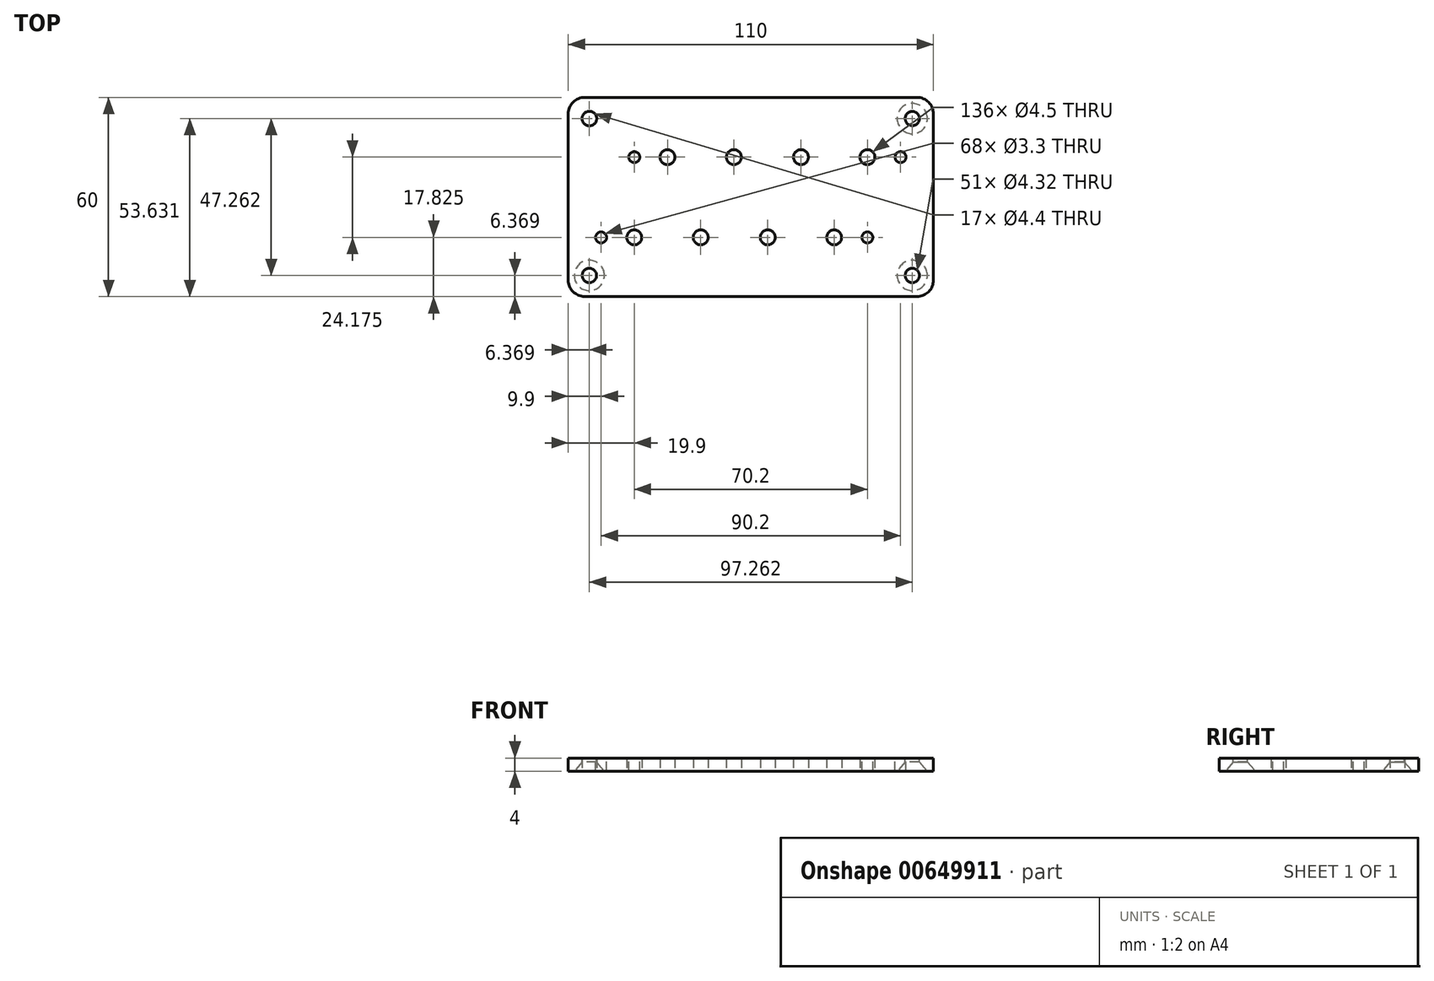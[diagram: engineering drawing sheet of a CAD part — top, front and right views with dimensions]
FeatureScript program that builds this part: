
annotation { "Feature Type Name" : "Feature", "Feature Type Description" : "" }
export const myFeature = defineFeature(function(context is Context, id is Id, definition is map)
    precondition{}
    {
        {
            var Q0;
            Q0=qCreatedBy(makeId("Top.planeOp"),FACE);
            var sketch = newSketch(context, id + "F0", { "sketchPlane" : qUnion([Q0])});
            skPoint(sketch, "E0.middle", {"position": v(5, 12) * mm});
            skCircle(sketch, "E1.MirrorC", {"center": v(-35.1, 12) * mm, "radius": 1.75 * mm});
            skLineSegment(sketch, "E2.bottom", {"start": v(40.1, 22) * mm, "end": v(-30.1, 22) * mm});
            skLineSegment(sketch, "E2.top", {"start": v(40.1, 2) * mm, "end": v(-30.1, 2) * mm});
            skLineSegment(sketch, "E2.left", {"start": v(46.36, 18.13) * mm, "end": v(46.36, 18.13) * mm});
            skLineSegment(sketch, "E2.right", {"start": v(-43.84, 18.13) * mm, "end": v(-43.84, 18.13) * mm});
            skPoint(sketch, "E3.visualSharp", {"position": v(50.1, 22) * mm});
            skArc(sketch, "E3.filletArc", {"start": v(50.1, 12) * mm, "mid": v(47.17, 19.07) * mm, "end": v(40.1, 22) * mm});
            skPoint(sketch, "E4.visualSharp", {"position": v(50.1, 2) * mm});
            skArc(sketch, "E4.filletArc", {"start": v(40.1, 2) * mm, "mid": v(47.17, 4.93) * mm, "end": v(50.1, 12) * mm});
            skPoint(sketch, "E5.visualSharp", {"position": v(-40.1, 2) * mm});
            skArc(sketch, "E5.filletArc", {"start": v(-40.1, 12) * mm, "mid": v(-37.17, 4.93) * mm, "end": v(-30.1, 2) * mm});
            skPoint(sketch, "E6.visualSharp", {"position": v(-40.1, 22) * mm});
            skArc(sketch, "E6.filletArc", {"start": v(-30.1, 22) * mm, "mid": v(-37.17, 19.07) * mm, "end": v(-40.1, 12) * mm});
            skCircle(sketch, "E7", {"center": v(-25.1, 12) * mm, "radius": 2.25 * mm});
            skCircle(sketch, "E8", {"center": v(-5.1, 12) * mm, "radius": 2.25 * mm});
            skCircle(sketch, "E9.MirrorC", {"center": v(35.1, 12) * mm, "radius": 2.25 * mm});
            skCircle(sketch, "E10.MirrorC", {"center": v(45.1, 12) * mm, "radius": 1.75 * mm});
            skCircle(sketch, "E11.MirrorC", {"center": v(15.1, 12) * mm, "radius": 2.25 * mm});
            skPoint(sketch, "E12.middle", {"position": v(-5, -12.18) * mm});
            skCircle(sketch, "E13.MirrorC", {"center": v(-45.1, -12.18) * mm, "radius": 1.75 * mm});
            skLineSegment(sketch, "E14.bottom", {"start": v(30.1, -2.18) * mm, "end": v(-40.1, -2.18) * mm});
            skLineSegment(sketch, "E14.top", {"start": v(30.1, -22.18) * mm, "end": v(-40.1, -22.18) * mm});
            skLineSegment(sketch, "E14.right", {"start": v(14.58, -2.05) * mm, "end": v(14.58, -2.05) * mm});
            skPoint(sketch, "E15.visualSharp", {"position": v(40.1, -2.18) * mm});
            skArc(sketch, "E15.filletArc", {"start": v(40.1, -12.18) * mm, "mid": v(37.17, -5.1) * mm, "end": v(30.1, -2.18) * mm});
            skPoint(sketch, "E16.visualSharp", {"position": v(40.1, -22.18) * mm});
            skArc(sketch, "E16.filletArc", {"start": v(30.1, -22.18) * mm, "mid": v(37.17, -19.25) * mm, "end": v(40.1, -12.18) * mm});
            skPoint(sketch, "E17.visualSharp", {"position": v(-50.1, -22.18) * mm});
            skArc(sketch, "E17.filletArc", {"start": v(-50.1, -12.18) * mm, "mid": v(-47.17, -19.25) * mm, "end": v(-40.1, -22.18) * mm});
            skPoint(sketch, "E18.visualSharp", {"position": v(-50.1, -2.18) * mm});
            skArc(sketch, "E18.filletArc", {"start": v(-40.1, -2.18) * mm, "mid": v(-47.17, -5.1) * mm, "end": v(-50.1, -12.18) * mm});
            skCircle(sketch, "E19", {"center": v(-35.1, -12.18) * mm, "radius": 2.25 * mm});
            skCircle(sketch, "E20", {"center": v(-15.1, -12.18) * mm, "radius": 2.25 * mm});
            skCircle(sketch, "E21.MirrorC", {"center": v(25.1, -12.18) * mm, "radius": 2.25 * mm});
            skCircle(sketch, "E22.MirrorC", {"center": v(35.1, -12.18) * mm, "radius": 1.75 * mm});
            skCircle(sketch, "E23.MirrorC", {"center": v(5.1, -12.18) * mm, "radius": 2.25 * mm});
            skLineSegment(sketch, "E24.bottom", {"start": v(50, 30) * mm, "end": v(-50, 30) * mm});
            skLineSegment(sketch, "E24.top", {"start": v(50, -30) * mm, "end": v(-50, -30) * mm});
            skLineSegment(sketch, "E24.left", {"start": v(55, 25) * mm, "end": v(55, -25) * mm});
            skLineSegment(sketch, "E24.right", {"start": v(-55, 25) * mm, "end": v(-55, -25) * mm});
            skPoint(sketch, "E24.middle", {"position": v(0, 0) * mm});
            skCircle(sketch, "E25", {"center": v(48.63, 23.63) * mm, "radius": 3.97 * mm});
            skCircle(sketch, "E26", {"center": v(48.63, 23.63) * mm, "radius": 2.2 * mm});
            skLineSegment(sketch, "E27", {"start": v(52.6, 23.63) * mm, "end": v(55, 23.63) * mm});
            skLineSegment(sketch, "E28", {"start": v(48.63, 27.6) * mm, "end": v(48.63, 30) * mm});
            skCircle(sketch, "E29.MirrorC", {"center": v(-48.63, 23.63) * mm, "radius": 3.97 * mm});
            skCircle(sketch, "E30.MirrorC", {"center": v(-48.63, 23.63) * mm, "radius": 2.2 * mm});
            skCircle(sketch, "E31.MirrorC", {"center": v(-48.63, -23.63) * mm, "radius": 2.2 * mm});
            skCircle(sketch, "E32.MirrorC", {"center": v(-48.63, -23.63) * mm, "radius": 3.97 * mm});
            skCircle(sketch, "E33.MirrorC", {"center": v(48.63, -23.63) * mm, "radius": 2.2 * mm});
            skCircle(sketch, "E34.MirrorC", {"center": v(48.63, -23.63) * mm, "radius": 3.97 * mm});
            skPoint(sketch, "E35.visualSharp", {"position": v(-55, 30) * mm});
            skArc(sketch, "E35.filletArc", {"start": v(-50, 30) * mm, "mid": v(-53.54, 28.54) * mm, "end": v(-55, 25) * mm});
            skPoint(sketch, "E36.visualSharp", {"position": v(55, 30) * mm});
            skArc(sketch, "E36.filletArc", {"start": v(55, 25) * mm, "mid": v(53.54, 28.54) * mm, "end": v(50, 30) * mm});
            skPoint(sketch, "E37.visualSharp", {"position": v(55, -30) * mm});
            skArc(sketch, "E37.filletArc", {"start": v(50, -30) * mm, "mid": v(53.54, -28.54) * mm, "end": v(55, -25) * mm});
            skPoint(sketch, "E38.visualSharp", {"position": v(-55, -30) * mm});
            skArc(sketch, "E38.filletArc", {"start": v(-55, -25) * mm, "mid": v(-53.54, -28.54) * mm, "end": v(-50, -30) * mm});
            skSolve(sketch);
        }
        {
            var Q0;
            Q0 = qSketchRegion(id + "F0", true);
            var Q1;
            Q1=makeQuery(id+"F0.imprint","IMPRINT",FACE,{"disambiguationData":[TD([[makeQuery(id+"F0.imprint","IMPRINT",EDGE,{"derivedFrom":sQuery(id+"F0.wireOp",EDGE,"E29.MirrorC")}),-1.0]])]});
            var Q2;
            Q2=makeQuery(id+"F0.imprint","IMPRINT",FACE,{"disambiguationData":[TD([[makeQuery(id+"F0.imprint","IMPRINT",EDGE,{"derivedFrom":sQuery(id+"F0.wireOp",EDGE,"E26")}),-1.0]])]});
            var Q3;
            Q3=makeQuery(id+"F0.imprint","IMPRINT",FACE,{"disambiguationData":[TD([[makeQuery(id+"F0.imprint","IMPRINT",EDGE,{"derivedFrom":sQuery(id+"F0.wireOp",EDGE,"E1.MirrorC")}),1.0]])]});
            var Q4;
            Q4=makeQuery(id+"F0.imprint","IMPRINT",FACE,{"disambiguationData":[TD([[makeQuery(id+"F0.imprint","IMPRINT",EDGE,{"derivedFrom":sQuery(id+"F0.wireOp",EDGE,"E13.MirrorC")}),1.0]])]});
            var Q5;
            Q5=makeQuery(id+"F0.imprint","IMPRINT",FACE,{"disambiguationData":[TD([[makeQuery(id+"F0.imprint","IMPRINT",EDGE,{"derivedFrom":sQuery(id+"F0.wireOp",EDGE,"E31.MirrorC")}),-1.0]])]});
            var Q6;
            Q6=makeQuery(id+"F0.imprint","IMPRINT",FACE,{"disambiguationData":[TD([[makeQuery(id+"F0.imprint","IMPRINT",EDGE,{"derivedFrom":sQuery(id+"F0.wireOp",EDGE,"E33.MirrorC")}),1.0]])]});
            var Q7;
            Q7=makeQuery(id+"F0.imprint","IMPRINT",FACE,{"disambiguationData":[TD([[makeQuery(id+"F0.imprint","IMPRINT",EDGE,{"derivedFrom":sQuery(id+"F0.wireOp",EDGE,"E31.MirrorC")}),1.0]])]});
            var Q8;
            Q8=makeQuery(id+"F0.imprint","IMPRINT",FACE,{"disambiguationData":[TD([[makeQuery(id+"F0.imprint","IMPRINT",EDGE,{"derivedFrom":sQuery(id+"F0.wireOp",EDGE,"E33.MirrorC")}),-1.0]])]});
            var Q9;
            Q9=makeQuery(id+"F0.imprint","IMPRINT",FACE,{"disambiguationData":[TD([[makeQuery(id+"F0.imprint","IMPRINT",EDGE,{"derivedFrom":sQuery(id+"F0.wireOp",EDGE,"E30.MirrorC")}),-1.0]])]});
            var Q10;
            Q10=makeQuery(id+"F0.imprint","IMPRINT",FACE,{"disambiguationData":[TD([[makeQuery(id+"F0.imprint","IMPRINT",EDGE,{"derivedFrom":sQuery(id+"F0.wireOp",EDGE,"E26")}),1.0]])]});
            var Q11;
            Q11=makeQuery(id+"F0.imprint","IMPRINT",FACE,{"disambiguationData":[TD([[makeQuery(id+"F0.imprint","IMPRINT",EDGE,{"derivedFrom":sQuery(id+"F0.wireOp",EDGE,"E10.MirrorC")}),1.0]])]});
            var Q12;
            Q12=makeQuery(id+"F0.imprint","IMPRINT",FACE,{"disambiguationData":[TD([[makeQuery(id+"F0.imprint","IMPRINT",EDGE,{"derivedFrom":sQuery(id+"F0.wireOp",EDGE,"E1.MirrorC")}),-1.0]])]});
            var Q13;
            Q13=makeQuery(id+"F0.imprint","IMPRINT",FACE,{"disambiguationData":[TD([[makeQuery(id+"F0.imprint","IMPRINT",EDGE,{"derivedFrom":sQuery(id+"F0.wireOp",EDGE,"E13.MirrorC")}),-1.0]])]});
            var Q14;
            Q14=makeQuery(id+"F0.imprint","IMPRINT",FACE,{"disambiguationData":[TD([[makeQuery(id+"F0.imprint","IMPRINT",EDGE,{"derivedFrom":sQuery(id+"F0.wireOp",EDGE,"E22.MirrorC")}),1.0]])]});
            extrude(context, id + "F1", {"entities" : qUnion([Q0, Q1, Q2, Q3, Q4, Q5, Q6, Q7, Q8, Q9, Q10, Q11, Q12, Q13, Q14]), "depth" : 4 * mm, "offsetDistance" : 25 * mm});
        }
        {
            var Q0;
            Q0=sQuery(id+"F0.wireOp",VERTEX,"E29.MirrorC.center");
            var Q1;
            Q1=sQuery(id+"F0.wireOp",VERTEX,"E31.MirrorC.center");
            var Q2;
            Q2=sQuery(id+"F0.wireOp",VERTEX,"E25.center");
            var Q3;
            Q3=sQuery(id+"F0.wireOp",VERTEX,"E33.MirrorC.center");
            var Q4;
            Q4=makeQuery(id+"F1.opExtrude","SWEPT_BODY",BODY,{"disambiguationData":[OSD([sQuery(id+"F0.wireOp",EDGE,"E1.MirrorC"),sQuery(id+"F0.wireOp",EDGE,"E7"),sQuery(id+"F0.wireOp",EDGE,"E8"),sQuery(id+"F0.wireOp",EDGE,"E9.MirrorC"),sQuery(id+"F0.wireOp",EDGE,"E10.MirrorC"),sQuery(id+"F0.wireOp",EDGE,"E11.MirrorC"),sQuery(id+"F0.wireOp",EDGE,"E13.MirrorC"),sQuery(id+"F0.wireOp",EDGE,"E19"),sQuery(id+"F0.wireOp",EDGE,"E20"),sQuery(id+"F0.wireOp",EDGE,"E21.MirrorC"),sQuery(id+"F0.wireOp",EDGE,"E22.MirrorC"),sQuery(id+"F0.wireOp",EDGE,"E23.MirrorC"),sQuery(id+"F0.wireOp",EDGE,"E24.bottom"),sQuery(id+"F0.wireOp",EDGE,"E24.top"),sQuery(id+"F0.wireOp",EDGE,"E24.left"),sQuery(id+"F0.wireOp",EDGE,"E24.right"),sQuery(id+"F0.wireOp",EDGE,"E26"),sQuery(id+"F0.wireOp",EDGE,"E30.MirrorC"),sQuery(id+"F0.wireOp",EDGE,"E31.MirrorC"),sQuery(id+"F0.wireOp",EDGE,"E33.MirrorC"),sQuery(id+"F0.wireOp",EDGE,"E35.filletArc"),sQuery(id+"F0.wireOp",EDGE,"E36.filletArc"),sQuery(id+"F0.wireOp",EDGE,"E37.filletArc"),sQuery(id+"F0.wireOp",EDGE,"E38.filletArc")])]});
            hole(context, id + "F2", {"style" : HoleStyle.C_SINK, "endStyle" : HoleEndStyle.THROUGH, "oppositeDirection" : true, "standardTappedOrClearance" : lookupTablePath({ "standard" : "ANSI", "fit" : "Close", "size" : "#8", "type" : "Clearance" }), "standardBlindInLast" : lookupTablePath({ "fit" : "Close", "standard" : "ANSI", "size" : "#8", "type" : "Clearance" }), "holeDiameter" : 4.32 * mm, "cSinkDiameter" : 9.12 * mm, "cSinkAngle" : 82 * degree, "majorDiameter" : 5 * mm, "isTappedThrough" : true, "tappedDepth" : 12 * mm, "tapClearance" : 3, "locations" : qUnion([Q0, Q1, Q2, Q3]), "scope" : qUnion([Q4])});
        }
        {
            var Q0;
            Q0=sQuery(id+"F0.wireOp",VERTEX,"E10.MirrorC.center");
            var Q1;
            Q1=sQuery(id+"F0.wireOp",VERTEX,"E1.MirrorC.center");
            var Q2;
            Q2=sQuery(id+"F0.wireOp",VERTEX,"E13.MirrorC.center");
            var Q3;
            Q3=sQuery(id+"F0.wireOp",VERTEX,"E22.MirrorC.center");
            var Q4;
            Q4=makeQuery(id+"F1.opExtrude","SWEPT_BODY",BODY,{"disambiguationData":[OSD([sQuery(id+"F0.wireOp",EDGE,"E7"),sQuery(id+"F0.wireOp",EDGE,"E8"),sQuery(id+"F0.wireOp",EDGE,"E9.MirrorC"),sQuery(id+"F0.wireOp",EDGE,"E11.MirrorC"),sQuery(id+"F0.wireOp",EDGE,"E19"),sQuery(id+"F0.wireOp",EDGE,"E20"),sQuery(id+"F0.wireOp",EDGE,"E21.MirrorC"),sQuery(id+"F0.wireOp",EDGE,"E23.MirrorC"),sQuery(id+"F0.wireOp",EDGE,"E24.bottom"),sQuery(id+"F0.wireOp",EDGE,"E24.top"),sQuery(id+"F0.wireOp",EDGE,"E24.left"),sQuery(id+"F0.wireOp",EDGE,"E24.right"),sQuery(id+"F0.wireOp",EDGE,"E35.filletArc"),sQuery(id+"F0.wireOp",EDGE,"E36.filletArc"),sQuery(id+"F0.wireOp",EDGE,"E37.filletArc"),sQuery(id+"F0.wireOp",EDGE,"E38.filletArc")])]});
            hole(context, id + "F3", {"style" : HoleStyle.SIMPLE, "endStyle" : HoleEndStyle.THROUGH, "oppositeDirection" : true, "standardTappedOrClearance" : lookupTablePath({ "standard" : "ISO", "engagement" : "75%", "pitch" : "0.7 mm", "size" : "M4", "type" : "Tapped" }), "standardBlindInLast" : lookupTablePath({ "standard" : "ISO", "engagement" : "75%", "pitch" : "0.7 mm", "size" : "M4", "type" : "Tapped" }), "holeDiameter" : 3.3 * mm, "majorDiameter" : 4 * mm, "showTappedDepth" : true, "isTappedThrough" : true, "tappedDepth" : 12 * mm, "tapClearance" : 3, "locations" : qUnion([Q0, Q1, Q2, Q3]), "scope" : qUnion([Q4])});
        }
    });
